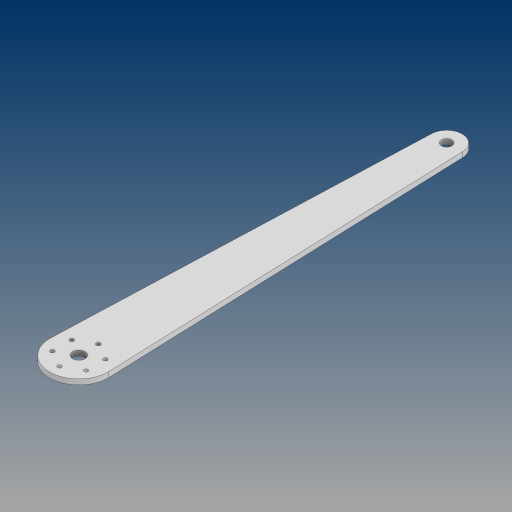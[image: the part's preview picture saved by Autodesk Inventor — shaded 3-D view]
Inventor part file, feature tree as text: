
AUTODESK INVENTOR PART (.ipt)
format: ipt  version: 2024.3 (Build 283343000, 343)  size: 113,664 bytes
history: native  units: in
note: dims shown in document units (in); Inventor stores cm internally (conversion verified against a paired STEP export)
features: extrude x1, sketch x1
ambient origin geometry x8: Origin, YZ Plane, XZ Plane, XY Plane, X Axis, Y Axis, Z Axis, Center Point
bodies: Solid1 (feature_tree)
feature tree (2):
  extrude  "Extrusion1"  Depth=0.25in
  sketch  "Sketch1"  dims[d0=17.8in d1=0.5in d2=0.6in d3=2.31in d4=0.25in d5=0.5in d6=1.875in d7=0.19in d8=2.3622in d10=360.0deg d12=0.25in d13=0.0in]
